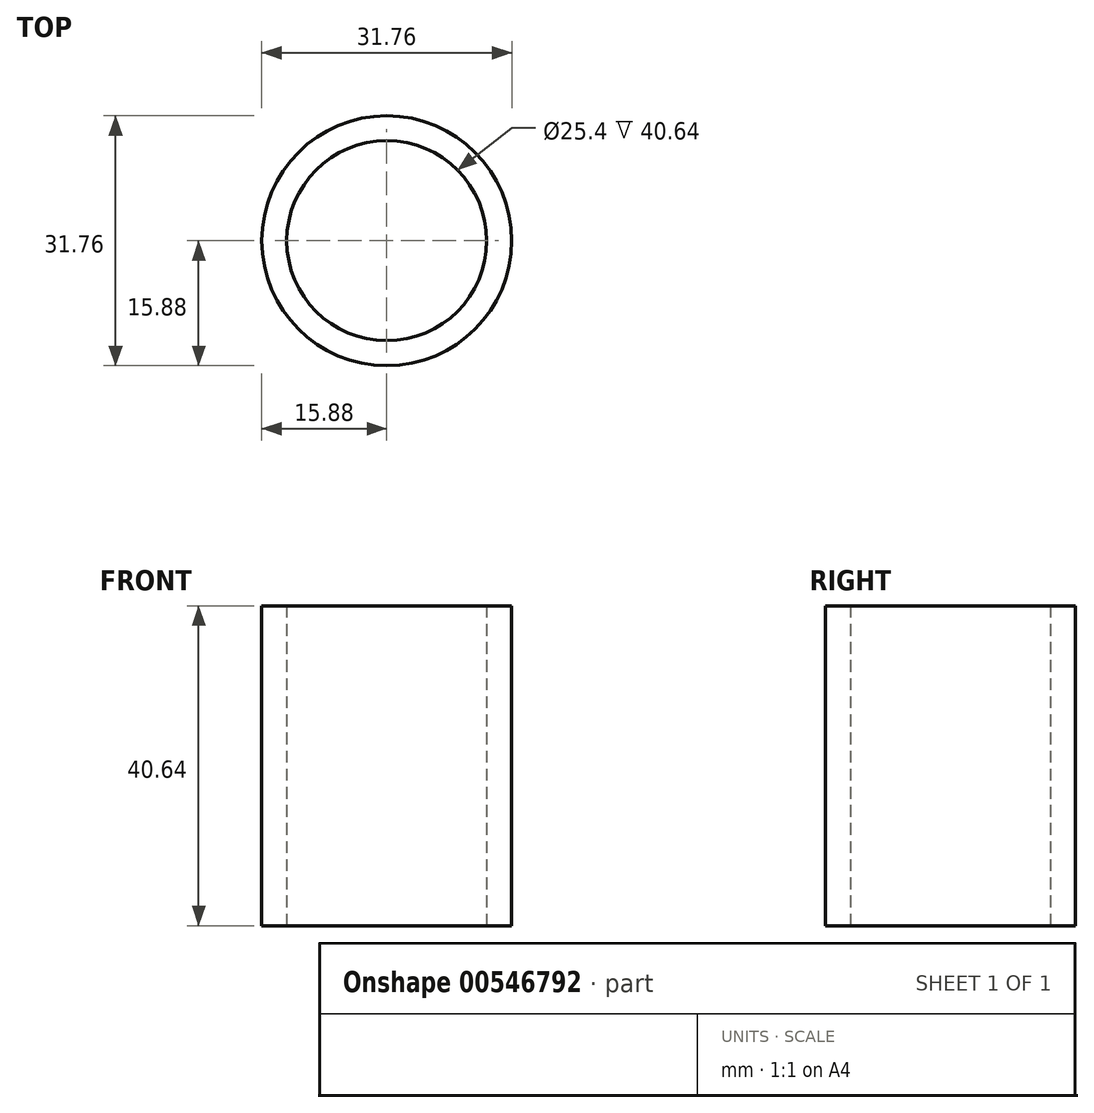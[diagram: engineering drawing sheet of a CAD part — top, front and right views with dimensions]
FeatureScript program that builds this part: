
annotation { "Feature Type Name" : "Feature", "Feature Type Description" : "" }
export const myFeature = defineFeature(function(context is Context, id is Id, definition is map)
    precondition{}
    {
        {
            var Q0;
            Q0=qCreatedBy(makeId("Top.planeOp"),FACE);
            var sketch = newSketch(context, id + "F0", { "sketchPlane" : qUnion([Q0])});
            skCircle(sketch, "E0", {"center": v(0, 0) * mm, "radius": 15.88 * mm});
            skCircle(sketch, "E1", {"center": v(0, 0) * mm, "radius": 12.7 * mm});
            skSolve(sketch);
        }
        {
            var Q0;
            Q0 = qSketchRegion(id + "F0", true);
            extrude(context, id + "F1", {"entities" : qUnion([Q0]), "depth" : 40.64 * mm, "offsetDistance" : 25.4 * mm});
        }
    });
